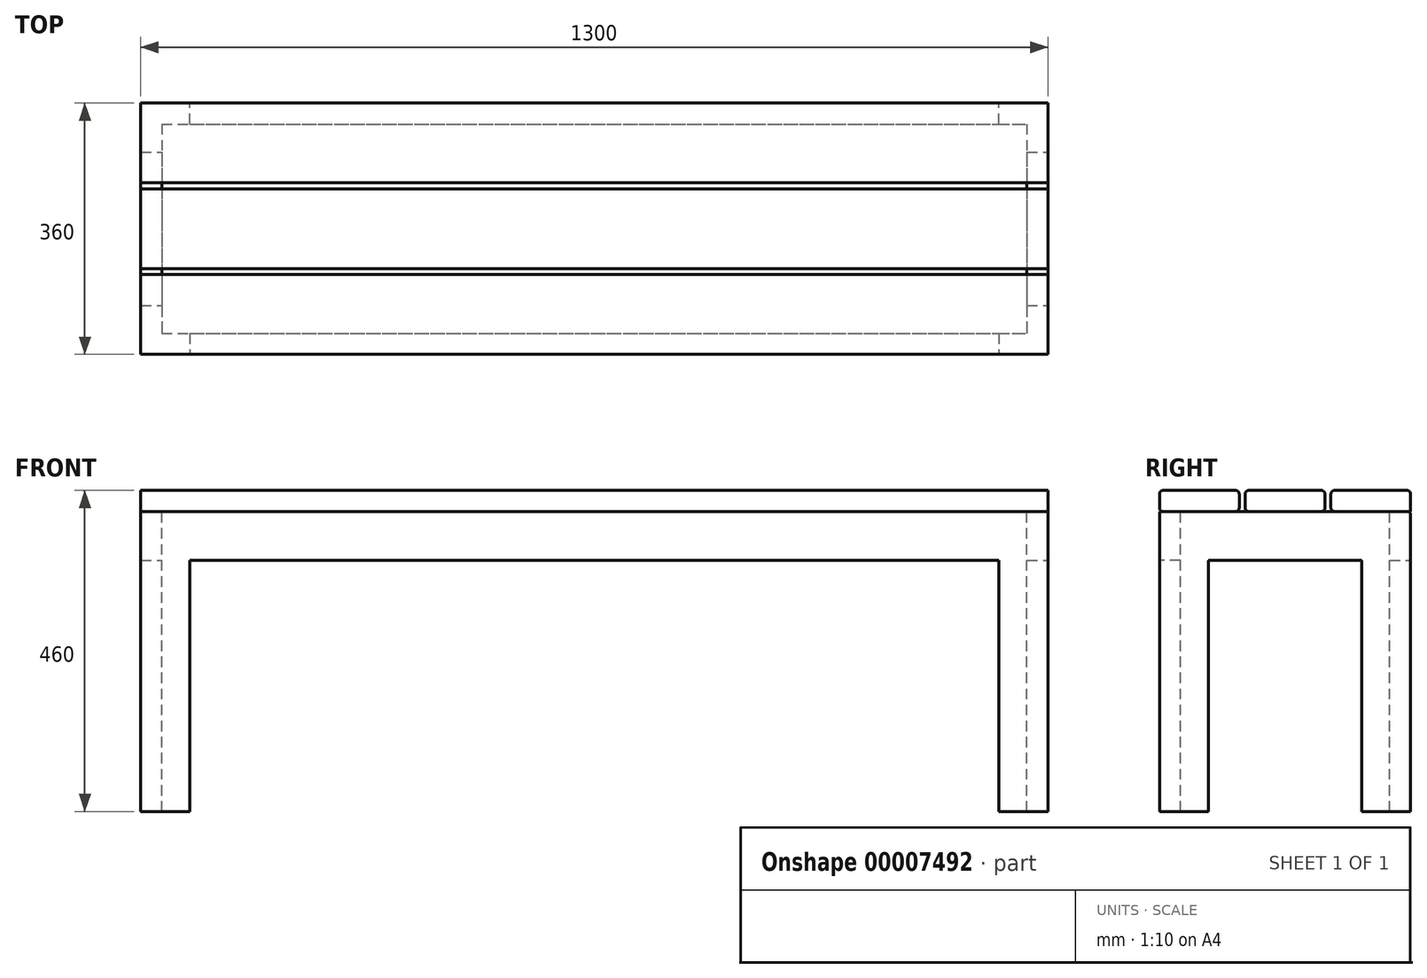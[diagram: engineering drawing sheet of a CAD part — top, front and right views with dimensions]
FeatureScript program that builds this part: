
annotation { "Feature Type Name" : "Feature", "Feature Type Description" : "" }
export const myFeature = defineFeature(function(context is Context, id is Id, definition is map)
    precondition{}
    {
        {
            var Q0;
            Q0=qCreatedBy(makeId("Top.planeOp"),FACE);
            var sketch = newSketch(context, id + "F0", { "sketchPlane" : qUnion([Q0])});
            skLineSegment(sketch, "E0.rect.bottom", {"start": v(-650, 180) * mm, "end": v(650, 180) * mm});
            skLineSegment(sketch, "E0.rect.top", {"start": v(-650, -180) * mm, "end": v(650, -180) * mm});
            skLineSegment(sketch, "E0.rect.left", {"start": v(-650, 180) * mm, "end": v(-650, -180) * mm});
            skLineSegment(sketch, "E0.rect.right", {"start": v(650, 180) * mm, "end": v(650, -180) * mm});
            skPoint(sketch, "E0.rect.middle", {"position": v(0, 0) * mm});
            skLineSegment(sketch, "E1.rect.bottom", {"start": v(-620, 150) * mm, "end": v(620, 150) * mm});
            skLineSegment(sketch, "E1.rect.top", {"start": v(-620, -150) * mm, "end": v(620, -150) * mm});
            skLineSegment(sketch, "E1.rect.left", {"start": v(-620, 150) * mm, "end": v(-620, -150) * mm});
            skLineSegment(sketch, "E1.rect.right", {"start": v(620, 150) * mm, "end": v(620, -150) * mm});
            skLineSegment(sketch, "E2", {"start": v(-650, -110) * mm, "end": v(-620, -110) * mm});
            skLineSegment(sketch, "E3", {"start": v(-580, -150) * mm, "end": v(-580, -180) * mm});
            skLineSegment(sketch, "E4", {"start": v(-650, 110) * mm, "end": v(-620, 110) * mm});
            skLineSegment(sketch, "E5", {"start": v(-580, 150) * mm, "end": v(-580, 180) * mm});
            skLineSegment(sketch, "E6", {"start": v(580, 150) * mm, "end": v(580, 180) * mm});
            skLineSegment(sketch, "E7", {"start": v(620, 110) * mm, "end": v(650, 110) * mm});
            skLineSegment(sketch, "E8", {"start": v(620, -110) * mm, "end": v(650, -110) * mm});
            skLineSegment(sketch, "E9", {"start": v(580, -150) * mm, "end": v(580, -180) * mm});
            skSolve(sketch);
        }
        {
            var Q0;
            {var subQ1=sQuery(id+"F0.wireOp",EDGE,"E2");Q0=makeQuery(id+"F0.imprint","IMPRINT",FACE,{"disambiguationData":[TD([[makeQuery(id+"F0.imprint","IMPRINT",EDGE,{"derivedFrom":subQ1}),-1.0]])]});}
            var Q1;
            {var subQ0=sQuery(id+"F0.wireOp",EDGE,"E4");Q1=makeQuery(id+"F0.imprint","IMPRINT",FACE,{"disambiguationData":[TD([[makeQuery(id+"F0.imprint","IMPRINT",EDGE,{"derivedFrom":subQ0}),1.0]])]});}
            var Q2;
            {var subQ1=sQuery(id+"F0.wireOp",EDGE,"E6");Q2=makeQuery(id+"F0.imprint","IMPRINT",FACE,{"disambiguationData":[TD([[makeQuery(id+"F0.imprint","IMPRINT",EDGE,{"derivedFrom":subQ1}),-1.0]])]});}
            var Q3;
            {var subQ1=sQuery(id+"F0.wireOp",EDGE,"E8");Q3=makeQuery(id+"F0.imprint","IMPRINT",FACE,{"disambiguationData":[TD([[makeQuery(id+"F0.imprint","IMPRINT",EDGE,{"derivedFrom":subQ1}),-1.0]])]});}
            extrude(context, id + "F1", {"entities" : qUnion([Q0, Q1, Q2, Q3]), "oppositeDirection" : true, "depth" : 430 * mm});
        }
        {
            var Q0;
            {var subQ1=sQuery(id+"F0.wireOp",EDGE,"E2");Q0=makeQuery(id+"F0.imprint","IMPRINT",FACE,{"disambiguationData":[TD([[makeQuery(id+"F0.imprint","IMPRINT",EDGE,{"derivedFrom":subQ1}),1.0]])]});}
            var Q1;
            {var subQ1=sQuery(id+"F0.wireOp",EDGE,"E5");Q1=makeQuery(id+"F0.imprint","IMPRINT",FACE,{"disambiguationData":[TD([[makeQuery(id+"F0.imprint","IMPRINT",EDGE,{"derivedFrom":subQ1}),-1.0]])]});}
            var Q2;
            {var subQ1=sQuery(id+"F0.wireOp",EDGE,"E3");Q2=makeQuery(id+"F0.imprint","IMPRINT",FACE,{"disambiguationData":[TD([[makeQuery(id+"F0.imprint","IMPRINT",EDGE,{"derivedFrom":subQ1}),1.0]])]});}
            var Q3;
            {var subQ1=sQuery(id+"F0.wireOp",EDGE,"E7");Q3=makeQuery(id+"F0.imprint","IMPRINT",FACE,{"disambiguationData":[TD([[makeQuery(id+"F0.imprint","IMPRINT",EDGE,{"derivedFrom":subQ1}),-1.0]])]});}
            extrude(context, id + "F2", {"entities" : qUnion([Q0, Q1, Q2, Q3]), "operationType" : NewBodyOperationType.ADD, "oppositeDirection" : true, "depth" : 70 * mm});
        }
        {
            var Q0;
            Q0=qCreatedBy(makeId("Top.planeOp"),FACE);
            var sketch = newSketch(context, id + "F3", { "sketchPlane" : qUnion([Q0])});
            skLineSegment(sketch, "E10.bottom", {"start": v(-650, -180) * mm, "end": v(650, -180) * mm});
            skLineSegment(sketch, "E10.top", {"start": v(-650, -65.7) * mm, "end": v(650, -65.7) * mm});
            skLineSegment(sketch, "E10.left", {"start": v(-650, -180) * mm, "end": v(-650, -65.7) * mm});
            skLineSegment(sketch, "E10.right", {"start": v(650, -180) * mm, "end": v(650, -65.7) * mm});
            skLineSegment(sketch, "E11.0.1.0", {"start": v(-650, -57.15) * mm, "end": v(-650, 57.15) * mm});
            skLineSegment(sketch, "E11.0.1.1", {"start": v(-650, -57.15) * mm, "end": v(650, -57.15) * mm});
            skLineSegment(sketch, "E11.0.1.2", {"start": v(-650, 57.15) * mm, "end": v(650, 57.15) * mm});
            skLineSegment(sketch, "E11.0.1.3", {"start": v(650, -57.15) * mm, "end": v(650, 57.15) * mm});
            skLineSegment(sketch, "E11.direction1", {"start": v(-650, -180) * mm, "end": v(-624.6, -180) * mm, "construction": true});
            skLineSegment(sketch, "E11.direction2", {"start": v(-650, -180) * mm, "end": v(-650, -57.15) * mm, "construction": true});
            skLineSegment(sketch, "E12.0.0.2", {"start": v(-650, 65.7) * mm, "end": v(-650, 180) * mm});
            skLineSegment(sketch, "E12.3.0.2", {"start": v(-650, 65.7) * mm, "end": v(650, 65.7) * mm});
            skLineSegment(sketch, "E12.6.0.2", {"start": v(-650, 180) * mm, "end": v(650, 180) * mm});
            skLineSegment(sketch, "E12.9.0.2", {"start": v(650, 65.7) * mm, "end": v(650, 180) * mm});
            skSolve(sketch);
        }
        {
            var Q0;
            Q0 = qSketchRegion(id + "F3", true);
            extrude(context, id + "F4", {"entities" : qUnion([Q0]), "depth" : 30 * mm});
        }
        {
            var Q0;
            Q0=makeQuery(id+"F4.opExtrude","CAP_EDGE",EDGE,{"disambiguationData":[OSD([sQuery(id+"F3.wireOp",EDGE,"E11.0.8.1")])],"isStart":false});
            var Q1;
            Q1=makeQuery(id+"F4.opExtrude","CAP_EDGE",EDGE,{"disambiguationData":[OSD([sQuery(id+"F3.wireOp",EDGE,"E11.0.10.1")])],"isStart":false});
            var Q2;
            Q2=makeQuery(id+"F4.opExtrude","CAP_EDGE",EDGE,{"disambiguationData":[OSD([sQuery(id+"F3.wireOp",EDGE,"E10.bottom")])],"isStart":false});
            var Q3;
            Q3=makeQuery(id+"F4.opExtrude","CAP_EDGE",EDGE,{"disambiguationData":[OSD([sQuery(id+"F3.wireOp",EDGE,"E11.0.2.1")])],"isStart":false});
            var Q4;
            Q4=makeQuery(id+"F4.opExtrude","CAP_EDGE",EDGE,{"disambiguationData":[OSD([sQuery(id+"F3.wireOp",EDGE,"E10.top")])],"isStart":false});
            var Q5;
            Q5=makeQuery(id+"F4.opExtrude","CAP_EDGE",EDGE,{"disambiguationData":[OSD([sQuery(id+"F3.wireOp",EDGE,"E11.0.6.1")])],"isStart":false});
            var Q6;
            Q6=makeQuery(id+"F4.opExtrude","CAP_EDGE",EDGE,{"disambiguationData":[OSD([sQuery(id+"F3.wireOp",EDGE,"E11.0.4.1")])],"isStart":false});
            var Q7;
            Q7=makeQuery(id+"F4.opExtrude","CAP_EDGE",EDGE,{"disambiguationData":[OSD([sQuery(id+"F3.wireOp",EDGE,"E11.0.2.2")])],"isStart":false});
            var Q8;
            Q8=makeQuery(id+"F4.opExtrude","CAP_EDGE",EDGE,{"disambiguationData":[OSD([sQuery(id+"F3.wireOp",EDGE,"E11.0.10.2")])],"isStart":false});
            var Q9;
            Q9=makeQuery(id+"F4.opExtrude","CAP_EDGE",EDGE,{"disambiguationData":[OSD([sQuery(id+"F3.wireOp",EDGE,"E11.0.8.2")])],"isStart":false});
            var Q10;
            Q10=makeQuery(id+"F4.opExtrude","CAP_EDGE",EDGE,{"disambiguationData":[OSD([sQuery(id+"F3.wireOp",EDGE,"E11.0.6.2")])],"isStart":false});
            var Q11;
            Q11=makeQuery(id+"F4.opExtrude","CAP_EDGE",EDGE,{"disambiguationData":[OSD([sQuery(id+"F3.wireOp",EDGE,"E11.0.4.2")])],"isStart":false});
            var Q12;
            Q12=makeQuery(id+"F4.opExtrude","CAP_EDGE",EDGE,{"disambiguationData":[OSD([sQuery(id+"F3.wireOp",EDGE,"E11.0.9.1")])],"isStart":false});
            var Q13;
            Q13=makeQuery(id+"F4.opExtrude","CAP_EDGE",EDGE,{"disambiguationData":[OSD([sQuery(id+"F3.wireOp",EDGE,"E11.0.7.1")])],"isStart":false});
            var Q14;
            Q14=makeQuery(id+"F4.opExtrude","CAP_EDGE",EDGE,{"disambiguationData":[OSD([sQuery(id+"F3.wireOp",EDGE,"E11.0.5.1")])],"isStart":false});
            var Q15;
            Q15=makeQuery(id+"F4.opExtrude","CAP_EDGE",EDGE,{"disambiguationData":[OSD([sQuery(id+"F3.wireOp",EDGE,"E11.0.3.1")])],"isStart":false});
            var Q16;
            Q16=makeQuery(id+"F4.opExtrude","CAP_EDGE",EDGE,{"disambiguationData":[OSD([sQuery(id+"F3.wireOp",EDGE,"E11.0.3.2")])],"isStart":false});
            var Q17;
            Q17=makeQuery(id+"F4.opExtrude","CAP_EDGE",EDGE,{"disambiguationData":[OSD([sQuery(id+"F3.wireOp",EDGE,"E11.0.1.2")])],"isStart":false});
            var Q18;
            Q18=makeQuery(id+"F4.opExtrude","CAP_EDGE",EDGE,{"disambiguationData":[OSD([sQuery(id+"F3.wireOp",EDGE,"E11.0.7.2")])],"isStart":false});
            var Q19;
            Q19=makeQuery(id+"F4.opExtrude","CAP_EDGE",EDGE,{"disambiguationData":[OSD([sQuery(id+"F3.wireOp",EDGE,"E11.0.9.2")])],"isStart":false});
            var Q20;
            Q20=makeQuery(id+"F4.opExtrude","CAP_EDGE",EDGE,{"disambiguationData":[OSD([sQuery(id+"F3.wireOp",EDGE,"E11.0.5.2")])],"isStart":false});
            var Q21;
            Q21=makeQuery(id+"F4.opExtrude","CAP_EDGE",EDGE,{"disambiguationData":[OSD([sQuery(id+"F3.wireOp",EDGE,"E11.0.1.1")])],"isStart":false});
            var Q22;
            Q22=makeQuery(id+"F4.opExtrude","CAP_EDGE",EDGE,{"disambiguationData":[OSD([sQuery(id+"F3.wireOp",EDGE,"E10.bottom")])],"isStart":true});
            var Q23;
            Q23=makeQuery(id+"F4.opExtrude","CAP_EDGE",EDGE,{"disambiguationData":[OSD([sQuery(id+"F3.wireOp",EDGE,"E11.0.5.1")])],"isStart":true});
            var Q24;
            Q24=makeQuery(id+"F4.opExtrude","CAP_EDGE",EDGE,{"disambiguationData":[OSD([sQuery(id+"F3.wireOp",EDGE,"E11.0.2.2")])],"isStart":true});
            var Q25;
            Q25=makeQuery(id+"F4.opExtrude","CAP_EDGE",EDGE,{"disambiguationData":[OSD([sQuery(id+"F3.wireOp",EDGE,"E11.0.6.2")])],"isStart":true});
            var Q26;
            Q26=makeQuery(id+"F4.opExtrude","CAP_EDGE",EDGE,{"disambiguationData":[OSD([sQuery(id+"F3.wireOp",EDGE,"E11.0.4.2")])],"isStart":true});
            var Q27;
            Q27=makeQuery(id+"F4.opExtrude","CAP_EDGE",EDGE,{"disambiguationData":[OSD([sQuery(id+"F3.wireOp",EDGE,"E11.0.10.2")])],"isStart":true});
            var Q28;
            Q28=makeQuery(id+"F4.opExtrude","CAP_EDGE",EDGE,{"disambiguationData":[OSD([sQuery(id+"F3.wireOp",EDGE,"E11.0.8.2")])],"isStart":true});
            var Q29;
            Q29=makeQuery(id+"F4.opExtrude","CAP_EDGE",EDGE,{"disambiguationData":[OSD([sQuery(id+"F3.wireOp",EDGE,"E11.0.8.1")])],"isStart":true});
            var Q30;
            Q30=makeQuery(id+"F4.opExtrude","CAP_EDGE",EDGE,{"disambiguationData":[OSD([sQuery(id+"F3.wireOp",EDGE,"E11.0.10.1")])],"isStart":true});
            var Q31;
            Q31=makeQuery(id+"F4.opExtrude","CAP_EDGE",EDGE,{"disambiguationData":[OSD([sQuery(id+"F3.wireOp",EDGE,"E11.0.6.1")])],"isStart":true});
            var Q32;
            Q32=makeQuery(id+"F4.opExtrude","CAP_EDGE",EDGE,{"disambiguationData":[OSD([sQuery(id+"F3.wireOp",EDGE,"E11.0.4.1")])],"isStart":true});
            var Q33;
            Q33=makeQuery(id+"F4.opExtrude","CAP_EDGE",EDGE,{"disambiguationData":[OSD([sQuery(id+"F3.wireOp",EDGE,"E11.0.2.1")])],"isStart":true});
            var Q34;
            Q34=makeQuery(id+"F4.opExtrude","CAP_EDGE",EDGE,{"disambiguationData":[OSD([sQuery(id+"F3.wireOp",EDGE,"E10.top")])],"isStart":true});
            var Q35;
            Q35=makeQuery(id+"F4.opExtrude","CAP_EDGE",EDGE,{"disambiguationData":[OSD([sQuery(id+"F3.wireOp",EDGE,"E11.0.7.1")])],"isStart":true});
            var Q36;
            Q36=makeQuery(id+"F4.opExtrude","CAP_EDGE",EDGE,{"disambiguationData":[OSD([sQuery(id+"F3.wireOp",EDGE,"E11.0.9.2")])],"isStart":true});
            var Q37;
            Q37=makeQuery(id+"F4.opExtrude","CAP_EDGE",EDGE,{"disambiguationData":[OSD([sQuery(id+"F3.wireOp",EDGE,"E11.0.7.2")])],"isStart":true});
            var Q38;
            Q38=makeQuery(id+"F4.opExtrude","CAP_EDGE",EDGE,{"disambiguationData":[OSD([sQuery(id+"F3.wireOp",EDGE,"E11.0.5.2")])],"isStart":true});
            var Q39;
            Q39=makeQuery(id+"F4.opExtrude","CAP_EDGE",EDGE,{"disambiguationData":[OSD([sQuery(id+"F3.wireOp",EDGE,"E11.0.3.1")])],"isStart":true});
            var Q40;
            Q40=makeQuery(id+"F4.opExtrude","CAP_EDGE",EDGE,{"disambiguationData":[OSD([sQuery(id+"F3.wireOp",EDGE,"E11.0.1.1")])],"isStart":true});
            var Q41;
            Q41=makeQuery(id+"F4.opExtrude","CAP_EDGE",EDGE,{"disambiguationData":[OSD([sQuery(id+"F3.wireOp",EDGE,"E11.0.9.1")])],"isStart":true});
            var Q42;
            Q42=makeQuery(id+"F4.opExtrude","CAP_EDGE",EDGE,{"disambiguationData":[OSD([sQuery(id+"F3.wireOp",EDGE,"E11.0.1.2")])],"isStart":true});
            var Q43;
            Q43=makeQuery(id+"F4.opExtrude","CAP_EDGE",EDGE,{"disambiguationData":[OSD([sQuery(id+"F3.wireOp",EDGE,"E11.0.3.2")])],"isStart":true});
            var Q44;
            Q44=makeQuery(id+"F4.opExtrude","CAP_EDGE",EDGE,{"disambiguationData":[OSD([sQuery(id+"F3.wireOp",EDGE,"E12.3.0.2")])],"isStart":false});
            var Q45;
            Q45=makeQuery(id+"F4.opExtrude","CAP_EDGE",EDGE,{"disambiguationData":[OSD([sQuery(id+"F3.wireOp",EDGE,"E12.6.0.2")])],"isStart":false});
            var Q46;
            {var subQ0=sQuery(id+"F0.wireOp",EDGE,"E0.rect.bottom");Q46=makeQuery(id+"F2.boolean.opBoolean","MERGE",EDGE,{"derivedFrom":[makeQuery(id+"F1.opExtrude","CAP_EDGE",EDGE,{"disambiguationData":[OSD([subQ0]),TDD([makeQuery(id+"F0.imprint","IMPRINT",EDGE,{"disambiguationData":[TD([[makeQuery(id+"F0.imprint","INTERSECT",VERTEX,{"derivedFrom":[subQ0,sQuery(id+"F0.wireOp",EDGE,"E0.rect.left")]}),-1.0]])],"derivedFrom":subQ0})])],"isStart":true}),makeQuery(id+"F1.opExtrude","CAP_EDGE",EDGE,{"disambiguationData":[OSD([subQ0]),TDD([makeQuery(id+"F0.imprint","IMPRINT",EDGE,{"disambiguationData":[TD([[makeQuery(id+"F0.imprint","INTERSECT",VERTEX,{"derivedFrom":[subQ0,sQuery(id+"F0.wireOp",EDGE,"E0.rect.right")]}),1.0]])],"derivedFrom":subQ0})])],"isStart":true}),makeQuery(id+"F2.opExtrude","CAP_EDGE",EDGE,{"disambiguationData":[OSD([subQ0])],"isStart":true})]});}
            var Q47;
            Q47=makeQuery(id+"F4.opExtrude","CAP_EDGE",EDGE,{"disambiguationData":[OSD([sQuery(id+"F3.wireOp",EDGE,"E12.3.0.2")])],"isStart":true});
            fillet(context, id + "F5", {"entities" : qUnion([Q0, Q1, Q2, Q3, Q4, Q5, Q6, Q7, Q8, Q9, Q10, Q11, Q12, Q13, Q14, Q15, Q16, Q17, Q18, Q19, Q20, Q21, Q22, Q23, Q24, Q25, Q26, Q27, Q28, Q29, Q30, Q31, Q32, Q33, Q34, Q35, Q36, Q37, Q38, Q39, Q40, Q41, Q42, Q43, Q44, Q45, Q46, Q47]), "radius" : 5.08 * mm, "tangentPropagation" : true, "allowEdgeOverflow" : false});
        }
    });
